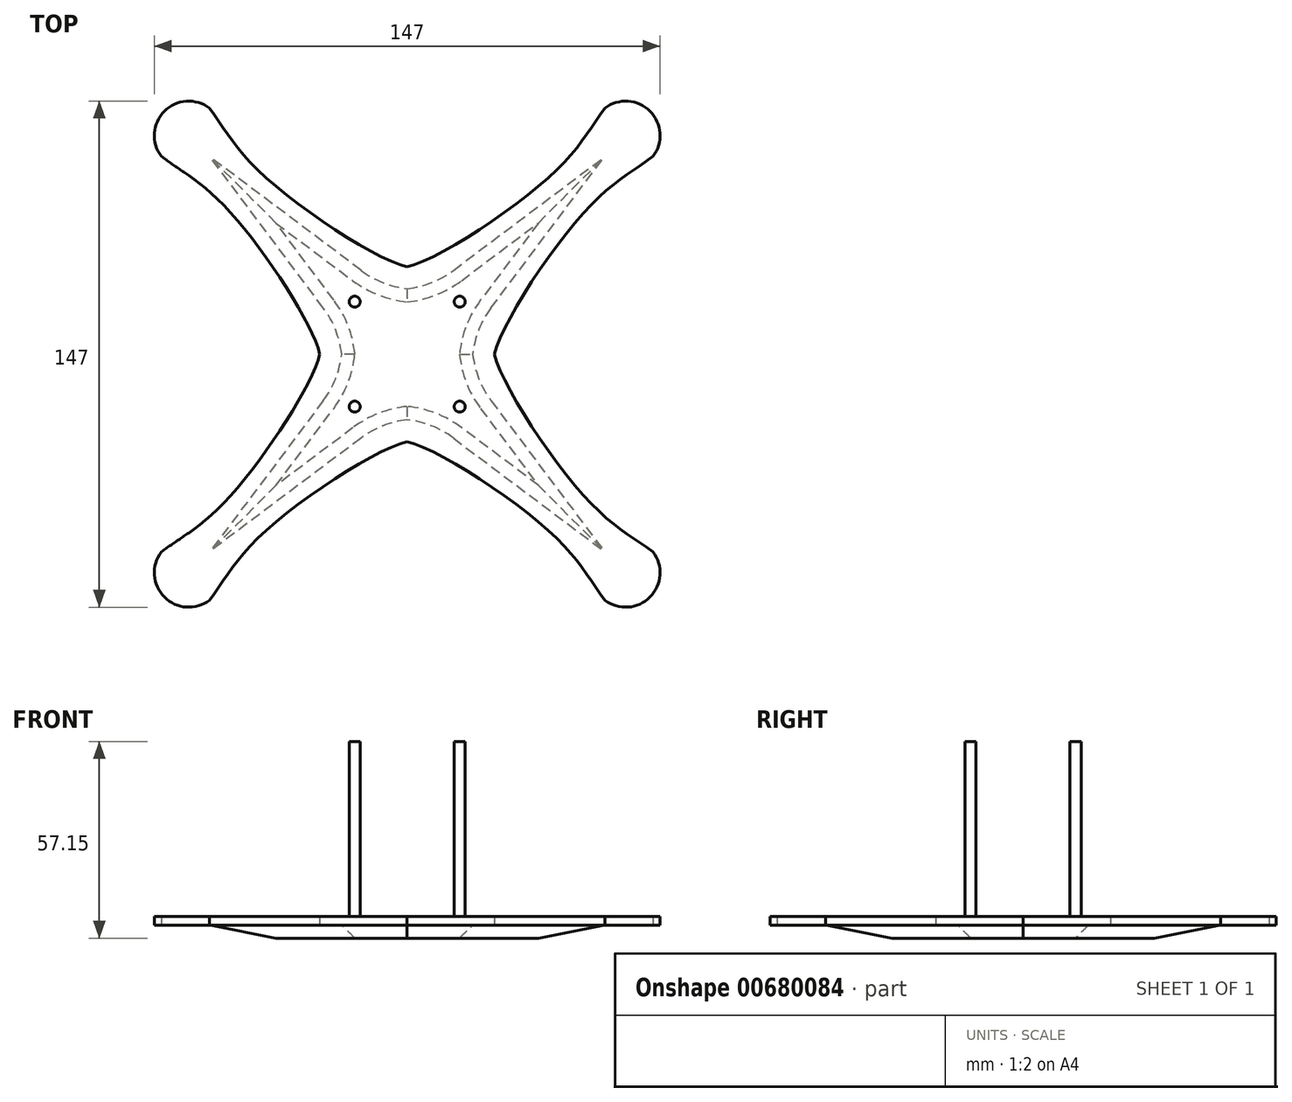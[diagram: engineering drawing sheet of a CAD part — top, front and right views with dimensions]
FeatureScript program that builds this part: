
annotation { "Feature Type Name" : "Feature", "Feature Type Description" : "" }
export const myFeature = defineFeature(function(context is Context, id is Id, definition is map)
    precondition{}
    {
        {
            var Q0;
            Q0=qCreatedBy(makeId("Top.planeOp"),FACE);
            var sketch = newSketch(context, id + "F0", { "sketchPlane" : qUnion([Q0])});
            skLineSegment(sketch, "E0", {"start": v(-50.8, 0) * mm, "end": v(50.8, 0) * mm, "construction": true});
            skLineSegment(sketch, "E1", {"start": v(0, 50.8) * mm, "end": v(0, -50.8) * mm, "construction": true});
            skLineSegment(sketch, "E2", {"start": v(0, 0) * mm, "end": v(-63.5, 63.5) * mm, "construction": true});
            skArc(sketch, "E3", {"start": v(-57.46, 71.47) * mm, "mid": v(-70.57, 70.57) * mm, "end": v(-71.47, 57.46) * mm});
            skLineSegment(sketch, "E4", {"start": v(0, 0) * mm, "end": v(0, 25.4) * mm});
            skFitSpline(sketch, "E5", {"points": [v(-57.46, 71.47) * mm, v(-42.48, 52.58) * mm, v(0, 25.4) * mm], "startDerivative": vector(33.33, -44.36) * mm, "endDerivative": vector(44.67, -9.8) * mm});
            skFitSpline(sketch, "E6.MirrorCS", {"points": [v(-71.47, 57.46) * mm, v(-52.58, 42.48) * mm, v(-25.4, 0) * mm], "startDerivative": vector(44.36, -33.33) * mm, "endDerivative": vector(9.8, -44.67) * mm});
            skFitSpline(sketch, "E7.MirrorCS", {"points": [v(-71.47, 57.46) * mm, v(-52.58, 42.48) * mm, v(-25.4, 0) * mm], "startDerivative": vector(44.36, -33.33) * mm, "endDerivative": vector(9.8, -44.67) * mm});
            skFitSpline(sketch, "E8.MirrorCS", {"points": [v(-57.46, 71.47) * mm, v(-42.48, 52.58) * mm, v(0, 25.4) * mm], "startDerivative": vector(33.33, -44.36) * mm, "endDerivative": vector(44.67, -9.8) * mm});
            skArc(sketch, "E9.MirrorCS", {"start": v(-71.47, 57.46) * mm, "mid": v(-70.57, 70.57) * mm, "end": v(-57.46, 71.47) * mm});
            skLineSegment(sketch, "E10.MirrorCS", {"start": v(0, 0) * mm, "end": v(-25.4, 0) * mm});
            skFitSpline(sketch, "E11.MirrorCS", {"points": [v(57.46, 71.47) * mm, v(42.48, 52.58) * mm, v(0, 25.4) * mm], "startDerivative": vector(-33.33, -44.36) * mm, "endDerivative": vector(-44.67, -9.8) * mm});
            skFitSpline(sketch, "E12.MirrorCS", {"points": [v(71.47, 57.46) * mm, v(52.58, 42.48) * mm, v(25.4, 0) * mm], "startDerivative": vector(-44.36, -33.33) * mm, "endDerivative": vector(-9.8, -44.67) * mm});
            skArc(sketch, "E13.MirrorCS", {"start": v(71.47, 57.46) * mm, "mid": v(70.57, 70.57) * mm, "end": v(57.46, 71.47) * mm});
            skFitSpline(sketch, "E14.MirrorCS", {"points": [v(-71.47, -57.46) * mm, v(-52.58, -42.48) * mm, v(-25.4, 0) * mm], "startDerivative": vector(44.36, 33.33) * mm, "endDerivative": vector(9.8, 44.67) * mm});
            skFitSpline(sketch, "E15.MirrorCS", {"points": [v(-57.46, -71.47) * mm, v(-42.48, -52.58) * mm, v(0, -25.4) * mm], "startDerivative": vector(33.33, 44.36) * mm, "endDerivative": vector(44.67, 9.8) * mm});
            skFitSpline(sketch, "E16.MirrorCS", {"points": [v(71.47, -57.46) * mm, v(52.58, -42.48) * mm, v(25.4, 0) * mm], "startDerivative": vector(-44.36, 33.33) * mm, "endDerivative": vector(-9.8, 44.67) * mm});
            skFitSpline(sketch, "E17.MirrorCS", {"points": [v(57.46, -71.47) * mm, v(42.48, -52.58) * mm, v(0, -25.4) * mm], "startDerivative": vector(-33.33, 44.36) * mm, "endDerivative": vector(-44.67, 9.8) * mm});
            skArc(sketch, "E18.MirrorCS", {"start": v(-71.47, -57.46) * mm, "mid": v(-70.57, -70.57) * mm, "end": v(-57.46, -71.47) * mm});
            skFitSpline(sketch, "E19.MirrorCS", {"points": [v(-71.47, -57.46) * mm, v(-52.58, -42.48) * mm, v(-25.4, 0) * mm], "startDerivative": vector(44.36, 33.33) * mm, "endDerivative": vector(9.8, 44.67) * mm});
            skArc(sketch, "E20.MirrorCS", {"start": v(-57.46, -71.47) * mm, "mid": v(-70.57, -70.57) * mm, "end": v(-71.47, -57.46) * mm});
            skArc(sketch, "E21.MirrorCS", {"start": v(71.47, -57.46) * mm, "mid": v(70.57, -70.57) * mm, "end": v(57.46, -71.47) * mm});
            skLineSegment(sketch, "E22.MirrorCS", {"start": v(0, 0) * mm, "end": v(0, -25.4) * mm});
            skLineSegment(sketch, "E23.MirrorCS", {"start": v(0, 0) * mm, "end": v(-63.5, -63.5) * mm, "construction": true});
            skLineSegment(sketch, "E24", {"start": v(-63.5, -63.5) * mm, "end": v(-63.5, 63.5) * mm});
            skSolve(sketch);
        }
        {
            var Q0;
            Q0=makeQuery(id+"F0.imprint","IMPRINT",FACE,{"disambiguationData":[TD([[makeQuery(id+"F0.imprint","IMPRINT",EDGE,{"derivedFrom":sQuery(id+"F0.wireOp",EDGE,"E4")}),-1.0]])]});
            var Q1;
            Q1=makeQuery(id+"F0.imprint","IMPRINT",FACE,{"disambiguationData":[TD([[makeQuery(id+"F0.imprint","IMPRINT",EDGE,{"derivedFrom":sQuery(id+"F0.wireOp",EDGE,"E10.MirrorCS")}),1.0]])]});
            var Q2;
            Q2=makeQuery(id+"F0.imprint","IMPRINT",FACE,{"disambiguationData":[TD([[makeQuery(id+"F0.imprint","IMPRINT",EDGE,{"derivedFrom":sQuery(id+"F0.wireOp",EDGE,"E4")}),1.0]])]});
            extrude(context, id + "F1", {"entities" : qUnion([Q0, Q1, Q2]), "depth" : 2.54 * mm, "offsetDistance" : 25.4 * mm, "symmetric" : true});
        }
        {
            var Q0;
            Q0=makeQuery(id+"F1.opExtrude","CAP_FACE",FACE,{"disambiguationData":[OSD([sQuery(id+"F0.wireOp",EDGE,"E7.MirrorCS"),sQuery(id+"F0.wireOp",EDGE,"E8.MirrorCS"),sQuery(id+"F0.wireOp",EDGE,"E9.MirrorCS"),sQuery(id+"F0.wireOp",EDGE,"E11.MirrorCS"),sQuery(id+"F0.wireOp",EDGE,"E12.MirrorCS"),sQuery(id+"F0.wireOp",EDGE,"E13.MirrorCS"),sQuery(id+"F0.wireOp",EDGE,"E16.MirrorCS"),sQuery(id+"F0.wireOp",EDGE,"E17.MirrorCS"),sQuery(id+"F0.wireOp",EDGE,"E15.MirrorCS"),sQuery(id+"F0.wireOp",EDGE,"E19.MirrorCS"),sQuery(id+"F0.wireOp",EDGE,"E20.MirrorCS"),sQuery(id+"F0.wireOp",EDGE,"E21.MirrorCS")])],"isStart":false});
            var sketch = newSketch(context, id + "F2", { "sketchPlane" : qUnion([Q0])});
            skCircle(sketch, "E25", {"center": v(15.25, 15.25) * mm, "radius": 1.6 * mm});
            skCircle(sketch, "E26.MirrorC", {"center": v(15.25, -15.25) * mm, "radius": 1.6 * mm});
            skCircle(sketch, "E27.MirrorC", {"center": v(-15.25, -15.25) * mm, "radius": 1.6 * mm});
            skCircle(sketch, "E28.MirrorC", {"center": v(-15.25, 15.25) * mm, "radius": 1.6 * mm});
            skSolve(sketch);
        }
        {
            var Q0;
            Q0 = qSketchRegion(id + "F2", true);
            extrude(context, id + "F3", {"entities" : qUnion([Q0]), "operationType" : NewBodyOperationType.ADD, "depth" : 50.8 * mm, "offsetDistance" : 25.4 * mm});
        }
        {
            var Q0;
            Q0=makeQuery(id+"F1.opExtrude","CAP_FACE",FACE,{"disambiguationData":[OSD([sQuery(id+"F0.wireOp",EDGE,"E7.MirrorCS"),sQuery(id+"F0.wireOp",EDGE,"E8.MirrorCS"),sQuery(id+"F0.wireOp",EDGE,"E9.MirrorCS"),sQuery(id+"F0.wireOp",EDGE,"E11.MirrorCS"),sQuery(id+"F0.wireOp",EDGE,"E12.MirrorCS"),sQuery(id+"F0.wireOp",EDGE,"E13.MirrorCS"),sQuery(id+"F0.wireOp",EDGE,"E16.MirrorCS"),sQuery(id+"F0.wireOp",EDGE,"E17.MirrorCS"),sQuery(id+"F0.wireOp",EDGE,"E15.MirrorCS"),sQuery(id+"F0.wireOp",EDGE,"E19.MirrorCS"),sQuery(id+"F0.wireOp",EDGE,"E20.MirrorCS"),sQuery(id+"F0.wireOp",EDGE,"E21.MirrorCS")])],"isStart":true});
            var sketch = newSketch(context, id + "F4", { "sketchPlane" : qUnion([Q0])});
            skLineSegment(sketch, "E29", {"start": v(-25.4, 0) * mm, "end": v(25.4, 0) * mm, "construction": true});
            skLineSegment(sketch, "E30", {"start": v(0, 25.4) * mm, "end": v(0, -25.4) * mm, "construction": true});
            skLineSegment(sketch, "E31", {"start": v(-25.4, 0) * mm, "end": v(0, 25.4) * mm, "construction": true});
            skPoint(sketch, "E32", {"position": v(-12.7, 12.7) * mm});
            skLineSegment(sketch, "E33", {"start": v(0, 0) * mm, "end": v(-25.4, 25.4) * mm, "construction": true});
            skPoint(sketch, "E34.middle", {"position": v(0, 0) * mm});
            skLineSegment(sketch, "E35", {"start": v(0, 0) * mm, "end": v(63.5, -63.5) * mm, "construction": true});
            skLineSegment(sketch, "E36", {"start": v(63.5, -63.5) * mm, "end": v(12.7, -25.4) * mm});
            skLineSegment(sketch, "E37", {"start": v(63.5, -63.5) * mm, "end": v(25.4, -12.7) * mm});
            skPoint(sketch, "E38.orphan", {"position": v(25.4, -25.4) * mm});
            skArc(sketch, "E39", {"start": v(12.7, -25.4) * mm, "mid": v(6.69, -22.02) * mm, "end": v(0, -20.32) * mm});
            skArc(sketch, "E40.MirrorCS", {"start": v(25.4, -12.7) * mm, "mid": v(22.02, -6.69) * mm, "end": v(20.32, 0) * mm});
            skArc(sketch, "E41.1.0", {"start": v(25.4, 12.7) * mm, "mid": v(22.02, 6.69) * mm, "end": v(20.32, 0) * mm});
            skLineSegment(sketch, "E41.1.1", {"start": v(63.5, 63.5) * mm, "end": v(25.4, 12.7) * mm});
            skLineSegment(sketch, "E41.1.2", {"start": v(63.5, 63.5) * mm, "end": v(12.7, 25.4) * mm});
            skArc(sketch, "E41.1.3", {"start": v(12.7, 25.4) * mm, "mid": v(6.69, 22.02) * mm, "end": v(0, 20.32) * mm});
            skArc(sketch, "E41.2.0", {"start": v(-12.7, 25.4) * mm, "mid": v(-6.69, 22.02) * mm, "end": v(0, 20.32) * mm});
            skLineSegment(sketch, "E41.2.1", {"start": v(-63.5, 63.5) * mm, "end": v(-12.7, 25.4) * mm});
            skLineSegment(sketch, "E41.2.2", {"start": v(-63.5, 63.5) * mm, "end": v(-25.4, 12.7) * mm});
            skArc(sketch, "E41.2.3", {"start": v(-25.4, 12.7) * mm, "mid": v(-22.02, 6.69) * mm, "end": v(-20.32, 0) * mm});
            skArc(sketch, "E41.3.0", {"start": v(-25.4, -12.7) * mm, "mid": v(-22.02, -6.69) * mm, "end": v(-20.32, 0) * mm});
            skLineSegment(sketch, "E41.3.1", {"start": v(-63.5, -63.5) * mm, "end": v(-25.4, -12.7) * mm});
            skLineSegment(sketch, "E41.3.2", {"start": v(-63.5, -63.5) * mm, "end": v(-12.7, -25.4) * mm});
            skArc(sketch, "E41.3.3", {"start": v(-12.7, -25.4) * mm, "mid": v(-6.69, -22.02) * mm, "end": v(0, -20.32) * mm});
            skSolve(sketch);
        }
        {
            var Q0;
            Q0 = qSketchRegion(id + "F4", true);
            extrude(context, id + "F5", {"entities" : qUnion([Q0]), "operationType" : NewBodyOperationType.ADD, "depth" : 3.8 * mm, "offsetDistance" : 25.4 * mm});
        }
        {
            var Q0;
            Q0=makeQuery(id+"F5.opExtrude","CAP_FACE",FACE,{"disambiguationData":[OSD([sQuery(id+"F4.wireOp",EDGE,"E36"),sQuery(id+"F4.wireOp",EDGE,"E37"),sQuery(id+"F4.wireOp",EDGE,"E39"),sQuery(id+"F4.wireOp",EDGE,"E40.MirrorCS"),sQuery(id+"F4.wireOp",EDGE,"E41.1.0"),sQuery(id+"F4.wireOp",EDGE,"E41.1.1"),sQuery(id+"F4.wireOp",EDGE,"E41.1.2"),sQuery(id+"F4.wireOp",EDGE,"E41.1.3"),sQuery(id+"F4.wireOp",EDGE,"E41.2.0"),sQuery(id+"F4.wireOp",EDGE,"E41.2.1"),sQuery(id+"F4.wireOp",EDGE,"E41.2.2"),sQuery(id+"F4.wireOp",EDGE,"E41.2.3"),sQuery(id+"F4.wireOp",EDGE,"E41.3.0"),sQuery(id+"F4.wireOp",EDGE,"E41.3.1"),sQuery(id+"F4.wireOp",EDGE,"E41.3.2"),sQuery(id+"F4.wireOp",EDGE,"E41.3.3")])],"isStart":false});
            chamfer(context, id + "F6", {"entities" : qUnion([Q0]), "width" : 5.08 * mm, "tangentPropagation" : true});
        }
    });
